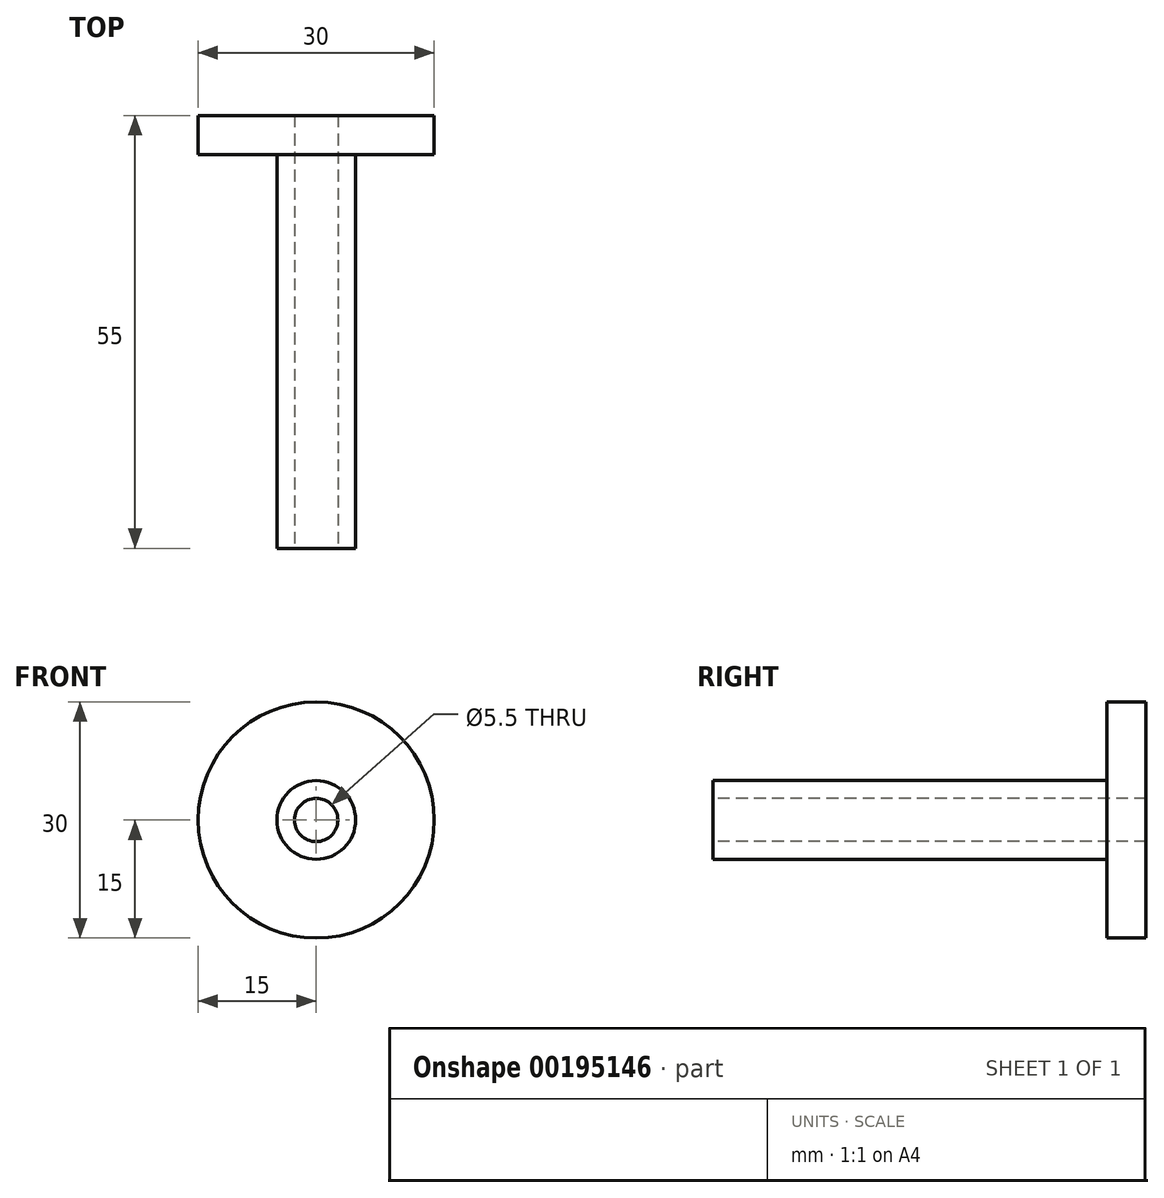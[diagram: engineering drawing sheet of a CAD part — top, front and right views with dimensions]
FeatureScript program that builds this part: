
annotation { "Feature Type Name" : "Feature", "Feature Type Description" : "" }
export const myFeature = defineFeature(function(context is Context, id is Id, definition is map)
    precondition{}
    {
        {
            var Q0;
            Q0=qCreatedBy(makeId("Front.planeOp"),FACE);
            var sketch = newSketch(context, id + "F0", { "sketchPlane" : qUnion([Q0])});
            skCircle(sketch, "E0", {"center": v(0, 0) * mm, "radius": 15 * mm});
            skSolve(sketch);
        }
        {
            var Q0;
            Q0=makeQuery(id+"F0.imprint","IMPRINT",FACE,{"disambiguationData":[TD([[makeQuery(id+"F0.imprint","IMPRINT",EDGE,{"derivedFrom":sQuery(id+"F0.wireOp",EDGE,"E0")}),1.0]])]});
            extrude(context, id + "F1", {"entities" : qUnion([Q0]), "depth" : 5 * mm});
        }
        {
            var Q0;
            Q0=makeQuery(id+"F1.opExtrude","CAP_FACE",FACE,{"disambiguationData":[OSD([sQuery(id+"F0.wireOp",EDGE,"E0")])],"isStart":false});
            var sketch = newSketch(context, id + "F2", { "sketchPlane" : qUnion([Q0])});
            skCircle(sketch, "E1", {"center": v(0, 0) * mm, "radius": 5 * mm});
            skSolve(sketch);
        }
        {
            var Q0;
            Q0 = qSketchRegion(id + "F2", true);
            extrude(context, id + "F3", {"entities" : qUnion([Q0]), "operationType" : NewBodyOperationType.ADD, "depth" : 50 * mm});
        }
        {
            var Q0;
            Q0=makeQuery(id+"F3.opExtrude","CAP_FACE",FACE,{"disambiguationData":[OSD([sQuery(id+"F2.wireOp",EDGE,"E1")])],"isStart":false});
            var sketch = newSketch(context, id + "F4", { "sketchPlane" : qUnion([Q0])});
            skPoint(sketch, "E2", {"position": v(0, 0) * mm});
            skSolve(sketch);
        }
        {
            var Q0;
            Q0=sQuery(id+"F4.wireOp",VERTEX,"E2");
            var Q1;
            Q1=makeQuery(id+"F1.opExtrude","SWEPT_BODY",BODY,{"disambiguationData":[OSD([sQuery(id+"F0.wireOp",EDGE,"E0")])]});
            hole(context, id + "F5", {"style" : HoleStyle.SIMPLE, "endStyle" : HoleEndStyle.THROUGH, "holeDiameter" : 5.5 * mm, "locations" : qUnion([Q0]), "scope" : qUnion([Q1]), "isTappedThrough" : true});
        }
    });
